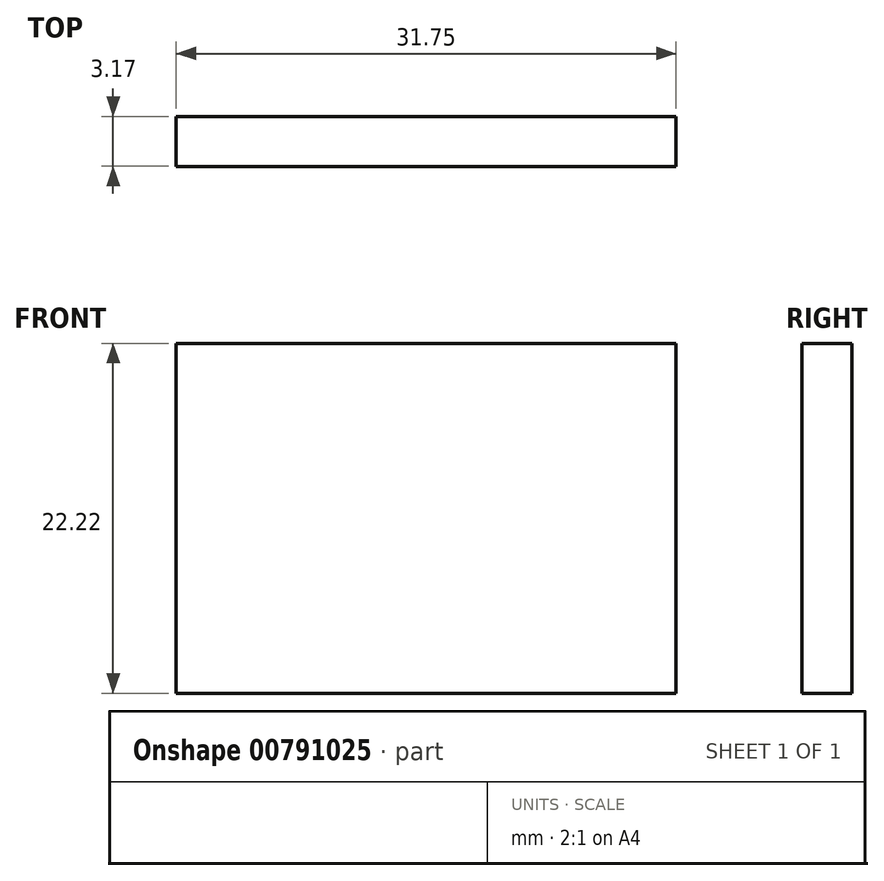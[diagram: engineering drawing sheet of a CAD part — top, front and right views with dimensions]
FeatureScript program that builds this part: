
annotation { "Feature Type Name" : "Feature", "Feature Type Description" : "" }
export const myFeature = defineFeature(function(context is Context, id is Id, definition is map)
    precondition{}
    {
        {
            var Q0;
            Q0=qCreatedBy(makeId("Front.planeOp"),FACE);
            var sketch = newSketch(context, id + "F0", { "sketchPlane" : qUnion([Q0])});
            skLineSegment(sketch, "E0.bottom", {"start": v(-17.5, 12.62) * mm, "end": v(14.24, 12.62) * mm});
            skLineSegment(sketch, "E0.top", {"start": v(-17.5, -9.6) * mm, "end": v(14.24, -9.6) * mm});
            skLineSegment(sketch, "E0.left", {"start": v(-17.5, 12.62) * mm, "end": v(-17.5, -9.6) * mm});
            skLineSegment(sketch, "E0.right", {"start": v(14.24, 12.62) * mm, "end": v(14.24, -9.6) * mm});
            skSolve(sketch);
        }
        {
            var Q0;
            Q0 = qSketchRegion(id + "F0", true);
            extrude(context, id + "F1", {"entities" : qUnion([Q0]), "depth" : 3.17 * mm, "offsetDistance" : 25.4 * mm});
        }
    });
